# Revit family: Рекуператор с промежуточным теплоносителем - вытяжная секция LITENED RGV
name_source: partatom
category: Оборудование
revit_build: Autodesk Revit 2017 (Build: 20160225_1515(x64)
units: mm (PartAtom-declared; Revit-internal decimal feet)

## family parameters
Всегда вертикально = Да
На основе рабочей плоскости = Нет
Общий = Нет
При загрузке вырезать с полостями = Нет
Размер круглого соединителя = Использовать диаметр
Тип детали = Нормальный
Точка расчета площади = Нет

## types (8) — shared parameters
h = 60 мм
Д = 610 мм
Д1 = 590 мм
Единица измерения = шт.
Завод изготовитель = NED
Ключевая пометка = Вентиляция
Наименование и тех.хар-ка = Рекуператор с промежуточным теплоносителем - вытяжная секция
Раздел = ОВ
высота ножек = 50 мм

## per-type parameters (varying)
| type | А | А1 | Б | Б1 | Г | Диаметр патрубков | Заправочный объем, л | Масса единицы | Материал | Мощность, кВт | Середина | Тип, марка, обозначение | высота | размер В | ширина |
| RGV 50-25 | 710 мм | 690 мм | 470 мм | 450 мм | 395 мм | 32 мм | 4.2 м³ | 43 | RAL 0000 Серый металл | 10 Вт | 295 мм | LITENED 50-25 RGV | 250 мм | 635 мм | 500 мм |
| RGV 50-30 | 710 мм | 690 мм | 520 мм | 500 мм | 445 мм | 38 мм | 4.9 м³ | 46 | Сталь серая | 12 Вт | 320 мм | LITENED 50-30 RGV | 300 мм | 635 мм | 500 мм |
| RGV 60-30 | 810 мм | 790 мм | 520 мм | 500 мм | 445 мм | 38 мм | 5.7 м³ | 51 | Сталь серая | 15 Вт | 320 мм | LITENED 60-30 RGV | 300 мм | 735 мм | 600 мм |
| RGV 60-35 | 810 мм | 790 мм | 570 мм | 550 мм | 495 мм | 51 мм | 7.1 м³ | 55 | Сталь серая | 17 Вт | 345 мм | LITENED 60-35 RGV | 350 мм | 735 мм | 600 мм |
| RGV 70-40 | 910 мм | 890 мм | 620 мм | 600 мм | 545 мм | 51 мм | 9.4 м³ | 65 | Сталь серая | 23 Вт | 370 мм | LITENED 70-40 RGV | 400 мм | 835 мм | 700 мм |
| RGV 80-50 | 1010 мм | 990 мм | 720 мм | 700 мм | 645 мм | 51 мм | 13.7 м³ | 82 | Сталь серая | 34 Вт | 420 мм | LITENED 80-50 RGV | 500 мм | 935 мм | 800 мм |
| RGV 90-50 | 1125 мм | 1105 мм | 740 мм | 720 мм | 645 мм | 51 мм | 15.3 м³ | 88 | Сталь серая | 39 Вт | 430 мм | LITENED 90-50 RGV | 500 мм | 1050 мм | 900 мм |
| RGV 100-50 | 1225 мм | 1205 мм | 740 мм | 720 мм | 665 мм | 51 мм | 16.8 м³ | 94 | Сталь серая | 43 Вт | 430 мм | LITENED 100-50 RGV | 500 мм | 1150 мм | 1000 мм |
